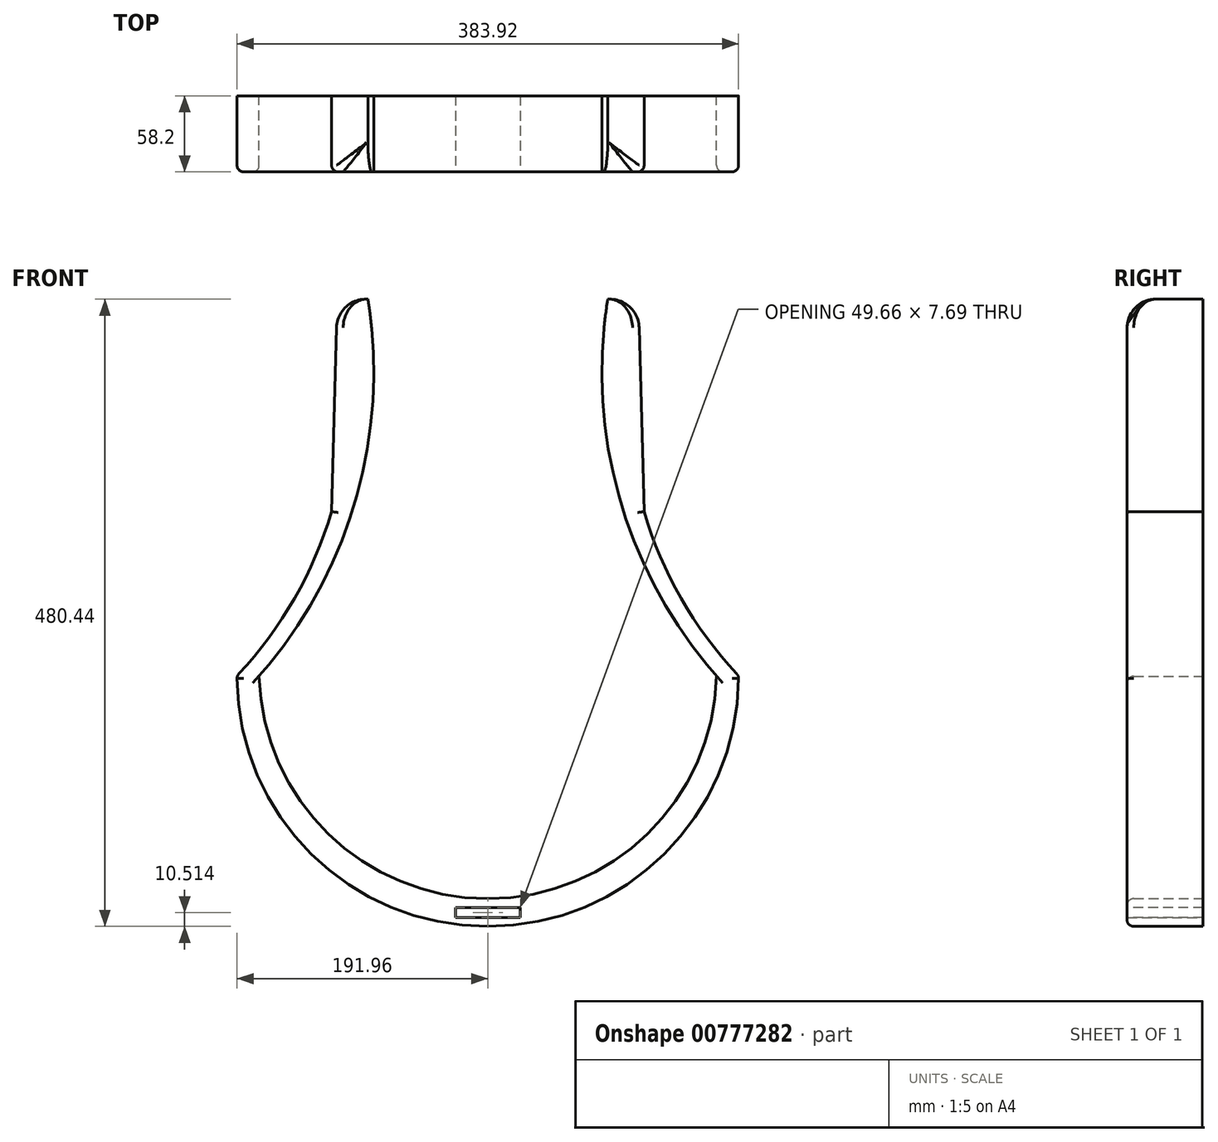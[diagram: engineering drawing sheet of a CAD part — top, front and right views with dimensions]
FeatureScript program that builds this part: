
annotation { "Feature Type Name" : "Feature", "Feature Type Description" : "" }
export const myFeature = defineFeature(function(context is Context, id is Id, definition is map)
    precondition{}
    {
        {
            var Q0;
            Q0=qCreatedBy(makeId("Front.planeOp"),FACE);
            var sketch = newSketch(context, id + "F0", { "sketchPlane" : qUnion([Q0])});
            skArc(sketch, "E0", {"start": v(-191.96, -89.52) * mm, "mid": v(-135.82, -225.33) * mm, "end": v(0, -281.43) * mm});
            skArc(sketch, "E1", {"start": v(-175.1, -89.75) * mm, "mid": v(0, -260.14) * mm, "end": v(175.1, -89.75) * mm});
            skArc(sketch, "E2", {"start": v(-175.1, -89.75) * mm, "mid": v(-101.15, 45.3) * mm, "end": v(-91.8, 198.98) * mm});
            skArc(sketch, "E3", {"start": v(-191.96, -89.52) * mm, "mid": v(-148.44, -30.92) * mm, "end": v(-119.61, 36.14) * mm});
            skArc(sketch, "E4.MirrorCS", {"start": v(175.1, -89.75) * mm, "mid": v(101.15, 45.3) * mm, "end": v(91.8, 198.98) * mm});
            skArc(sketch, "E5.MirrorCS", {"start": v(191.96, -89.52) * mm, "mid": v(148.44, -30.92) * mm, "end": v(119.61, 36.14) * mm});
            skPoint(sketch, "E6.MirrorCS.start.orphan", {"position": v(106.64, 258.14) * mm});
            skPoint(sketch, "E7.MirrorCS.end.orphan", {"position": v(135.7, 258.14) * mm});
            skLineSegment(sketch, "E8", {"start": v(-135.7, 258.14) * mm, "end": v(-135.7, 280.4) * mm});
            skPoint(sketch, "E9.end.orphan", {"position": v(0, 258.14) * mm});
            skPoint(sketch, "E10.orphan", {"position": v(0, -187.37) * mm});
            skPoint(sketch, "E11.start.orphan", {"position": v(0, -345.2) * mm});
            skLineSegment(sketch, "E12", {"start": v(119.61, 36.14) * mm, "end": v(115.28, 199.6) * mm});
            skLineSegment(sketch, "E13", {"start": v(115.28, 199.6) * mm, "end": v(91.8, 198.98) * mm});
            skLineSegment(sketch, "E14.MirrorCS", {"start": v(-119.61, 36.14) * mm, "end": v(-115.28, 199.6) * mm});
            skLineSegment(sketch, "E15.MirrorCS", {"start": v(-115.28, 199.6) * mm, "end": v(-91.8, 198.98) * mm});
            skPoint(sketch, "E16.orphan", {"position": v(-106.64, 258.14) * mm});
            skArc(sketch, "E17.MirrorCS", {"start": v(191.96, -89.52) * mm, "mid": v(0.51, -281.43) * mm, "end": v(-191.24, -89.82) * mm});
            skLineSegment(sketch, "E18", {"start": v(0, -345.2) * mm, "end": v(0, -281.43) * mm});
            skLineSegment(sketch, "E19.trimOffspring", {"start": v(0, -260.14) * mm, "end": v(0, -187.37) * mm});
            skSolve(sketch);
        }
        {
            var Q0;
            {var subQ3=sQuery(id+"F0.wireOp",EDGE,"E0");Q0=makeQuery(id+"F0.imprint","IMPRINT",FACE,{"disambiguationData":[TD([[makeQuery(id+"F0.imprint","IMPRINT",EDGE,{"derivedFrom":subQ3}),1.0]])]});}
            extrude(context, id + "F1", {"entities" : qUnion([Q0]), "depth" : 58.2 * mm, "offsetDistance" : 25 * mm});
        }
        {
            var Q0;
            Q0=makeQuery(id+"F1.opExtrude","CAP_FACE",FACE,{"disambiguationData":[OSD([sQuery(id+"F0.wireOp",EDGE,"E0"),sQuery(id+"F0.wireOp",EDGE,"E1"),sQuery(id+"F0.wireOp",EDGE,"E3"),sQuery(id+"F0.wireOp",EDGE,"E4.MirrorCS"),sQuery(id+"F0.wireOp",EDGE,"E5.MirrorCS"),sQuery(id+"F0.wireOp",EDGE,"E12"),sQuery(id+"F0.wireOp",EDGE,"E13"),sQuery(id+"F0.wireOp",EDGE,"E14.MirrorCS"),sQuery(id+"F0.wireOp",EDGE,"E2"),sQuery(id+"F0.wireOp",EDGE,"E15.MirrorCS"),sQuery(id+"F0.wireOp",EDGE,"E17.MirrorCS")])],"isStart":false});
            var sketch = newSketch(context, id + "F2", { "sketchPlane" : qUnion([Q0])});
            skLineSegment(sketch, "E20", {"start": v(0, -267.07) * mm, "end": v(24.83, -267.07) * mm});
            skLineSegment(sketch, "E21", {"start": v(24.83, -274.76) * mm, "end": v(0, -274.76) * mm});
            skLineSegment(sketch, "E22.MirrorCS", {"start": v(0, -267.07) * mm, "end": v(-24.83, -267.07) * mm});
            skLineSegment(sketch, "E23.MirrorCS", {"start": v(-24.83, -274.76) * mm, "end": v(0, -274.76) * mm});
            skLineSegment(sketch, "E24.trimOffspring", {"start": v(0, -267.07) * mm, "end": v(0, -260.14) * mm});
            skPoint(sketch, "E25.MirrorCS.start.orphan", {"position": v(-24.83, -267.07) * mm});
            skLineSegment(sketch, "E26", {"start": v(-24.83, -267.07) * mm, "end": v(-24.83, -274.76) * mm});
            skLineSegment(sketch, "E27", {"start": v(24.83, -267.07) * mm, "end": v(24.83, -274.76) * mm});
            skSolve(sketch);
        }
        {
            var Q0;
            Q0=makeQuery(id+"F1.opExtrude","CAP_EDGE",EDGE,{"disambiguationData":[OSD([sQuery(id+"F0.wireOp",EDGE,"E17.MirrorCS")])],"isStart":false});
            fillet(context, id + "F3", {"entities" : qUnion([Q0]), "radius" : 5 * mm, "tangentPropagation" : true, "allowEdgeOverflow" : false});
        }
        {
            var Q0;
            Q0=makeQuery(id+"F1.opExtrude","CAP_EDGE",EDGE,{"disambiguationData":[OSD([sQuery(id+"F0.wireOp",EDGE,"E1")])],"isStart":false});
            fillet(context, id + "F4", {"entities" : qUnion([Q0]), "radius" : 5 * mm, "tangentPropagation" : true, "allowEdgeOverflow" : false});
        }
        {
            var Q0;
            Q0=makeQuery(id+"F1.opExtrude","CAP_EDGE",EDGE,{"disambiguationData":[OSD([sQuery(id+"F0.wireOp",EDGE,"E5.MirrorCS")])],"isStart":false});
            fillet(context, id + "F5", {"entities" : qUnion([Q0]), "radius" : 5 * mm, "tangentPropagation" : true, "allowEdgeOverflow" : false});
        }
        {
            var Q0;
            Q0=makeQuery(id+"F1.opExtrude","CAP_EDGE",EDGE,{"disambiguationData":[OSD([sQuery(id+"F0.wireOp",EDGE,"E3")])],"isStart":false});
            fillet(context, id + "F6", {"entities" : qUnion([Q0]), "radius" : 5 * mm, "tangentPropagation" : true, "allowEdgeOverflow" : false});
        }
        {
            var Q0;
            Q0=makeQuery(id+"F1.opExtrude","CAP_EDGE",EDGE,{"disambiguationData":[OSD([sQuery(id+"F0.wireOp",EDGE,"E14.MirrorCS")])],"isStart":false});
            fillet(context, id + "F7", {"entities" : qUnion([Q0]), "radius" : 5.07 * mm, "tangentPropagation" : true, "allowEdgeOverflow" : false});
        }
        {
            var Q0;
            Q0=makeQuery(id+"F1.opExtrude","CAP_EDGE",EDGE,{"disambiguationData":[OSD([sQuery(id+"F0.wireOp",EDGE,"E12")])],"isStart":false});
            fillet(context, id + "F8", {"entities" : qUnion([Q0]), "radius" : 5.07 * mm, "tangentPropagation" : true, "allowEdgeOverflow" : false});
        }
        {
            var Q0;
            Q0=makeQuery(id+"F1.opExtrude","SWEPT_EDGE",EDGE,{"disambiguationData":[OSD([sQuery(id+"F0.wireOp",EDGE,"E12"),sQuery(id+"F0.wireOp",EDGE,"E13")])]});
            fillet(context, id + "F9", {"entities" : qUnion([Q0]), "radius" : 22.45 * mm, "tangentPropagation" : true, "allowEdgeOverflow" : false});
        }
        {
            var Q0;
            Q0=makeQuery(id+"F1.opExtrude","SWEPT_EDGE",EDGE,{"disambiguationData":[OSD([sQuery(id+"F0.wireOp",EDGE,"E14.MirrorCS"),sQuery(id+"F0.wireOp",EDGE,"E15.MirrorCS")])]});
            fillet(context, id + "F10", {"entities" : qUnion([Q0]), "radius" : 22.45 * mm, "tangentPropagation" : true, "allowEdgeOverflow" : false});
        }
        {
            var Q0;
            Q0=makeQuery(id+"F2.imprint","IMPRINT",FACE,{"disambiguationData":[TD([[makeQuery(id+"F2.imprint","IMPRINT",EDGE,{"derivedFrom":sQuery(id+"F2.wireOp",EDGE,"E20")}),-1.0]])]});
            extrude(context, id + "F11", {"entities" : qUnion([Q0]), "operationType" : NewBodyOperationType.REMOVE, "oppositeDirection" : true, "depth" : 103 * mm, "offsetDistance" : 25 * mm});
        }
    });
